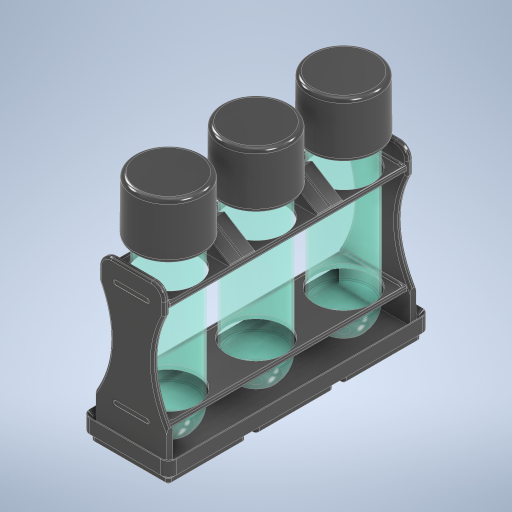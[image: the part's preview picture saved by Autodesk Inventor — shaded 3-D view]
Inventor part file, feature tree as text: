
AUTODESK INVENTOR PART (.ipt)
format: ipt  version: 2023 (Build 270158030, 158C)  size: 1,590,272 bytes
history: native  units: mm
features: extrude x23, sketch x21, other x17, fillet x17, projected_geometry x8, plane x6, chamfer x4, pattern_linear x3, mirror x2
ambient origin geometry x8: Origin, YZ Plane, XZ Plane, XY Plane, X Axis, Y Axis, Z Axis, Center Point
bodies: Body1 (feature_tree), Body2 (feature_tree), Body3 (feature_tree), Body4 (feature_tree), Body5 (feature_tree), Body6 (feature_tree), Body7 (feature_tree), Body8 (feature_tree), Body9 (feature_tree), Body10 (feature_tree), Body11 (feature_tree)
feature tree (101):
  other  "rack"
  extrude  "base-generic"  Depth=41.5mm
  extrude  "Extrusion8"  Depth=2.25mm TaperAngle=0.0deg
  extrude  "Extrusion9"  Depth=2.15mm
  extrude  "Extrusion10"  Depth=0.8mm
  extrude  "Extrusion11"  Depth=7.75mm
  extrude  "Extrusion12"  Depth=7.75mm
  plane  "Work Plane3"
  extrude  "Extrusion15"  Depth=2.4mm TaperAngle=0.0deg
  fillet  "Fillet3"  Radius=3.0mm
  extrude  "Extrusion16"  Depth=10.0mm
  fillet  "Fillet4"  Radius=2.25mm
  extrude  "Extrusion17"  Depth=35.592094mm
  fillet  "Fillet5"  Radius=15.0mm
  pattern_linear  "Rectangular Pattern1"  Spacing1=20.75mm  [1 undecoded]
  plane  "Work Plane8"
  sketch  "Sketch17"  dims[d66=7.75mm d67=2.4mm d68=0.0mm d69=3.0mm]
  extrude  "Extrusion18"  Depth=0.3mm
  pattern_linear  "Rectangular Pattern2"  Spacing1=26.75mm  [1 undecoded]
  plane  "Work Plane4"
  extrude  "Extrusion19"  Depth=2.0mm
  plane  "Work Plane6"
  extrude  "Extrusion21"  Depth=0.3mm
  extrude  "Extrusion20"  Depth=0.3mm TaperAngle=0.0deg
  fillet  "Fillet6"  Radius=9.0mm
  extrude  "Extrusion22"  Depth=0.3mm TaperAngle=0.0deg
  fillet  "Fillet7"  Radius=30.0mm
  extrude  "Extrusion28"  Depth=0.3mm
  fillet  "Fillet14"  Radius=1.0mm
  fillet  "Fillet15"  Radius=1.0mm
  pattern_linear  "Rectangular Pattern3"  Spacing1=68.75mm  [1 undecoded]
  extrude  "Extrusion23"  Depth=2.0mm
  extrude  "Extrusion24"  Depth=0.3mm
  extrude  "Extrusion25"  Depth=2.0mm TaperAngle=0.0deg
  extrude  "Extrusion26"  Depth=0.3mm
  fillet  "Fillet9"  Radius=55.0mm
  mirror  "Mirror2"
  fillet  "Fillet10"  Radius=73.0mm
  fillet  "Fillet13"  Radius=46.0mm
  extrude  "Extrusion27"  Depth=2.0mm TaperAngle=0.0deg
  chamfer  "Chamfer3"  Distance=6.0mm
  chamfer  "Chamfer4"  [1 undecoded]
  fillet  "Fillet12"  Radius=6.9mm
  fillet  "Fillet16"  Radius=6.9mm
  extrude  "Extrusion29"  Depth=0.3mm
  chamfer  "Chamfer5"  Distance=2.0mm
  chamfer  "Chamfer6"  Distance=1.0mm
  extrude  "Extrusion30"  Depth=0.3mm
  plane  "Work Plane9"
  mirror  "Mirror4"
  fillet  "Fillet19"  Radius=50.0mm
  fillet  "Fillet20"  Radius=14.0mm
  fillet  "Fillet21"  Radius=14.0mm
  fillet  "Fillet22"  Radius=3.1mm
  fillet  "Fillet18"  Radius=6.0mm
  extrude  "fill-gaps"  Depth=0.3mm
  sketch  "Sketch9"  dims[d50=41.5mm d51=41.5mm]
  sketch  "Sketch10"  dims[d52=3.75mm d53=2.25mm d54=0.0mm]
  projected_geometry  "Projected Loop2"
  sketch  "Sketch11"  dims[d55=3.75mm d56=2.15mm d57=-7.853982mm]
  projected_geometry  "Projected Loop3"
  sketch  "Sketch12"  dims[d58=1.8mm d59=0.0mm d60=0.8mm d61=-7.853982mm]
  projected_geometry  "Projected Loop4"
  sketch  "Sketch13"  dims[d62=6.5mm d63=7.75mm]
  sketch  "Sketch14"  dims[d64=7.75mm d65=7.75mm]
  sketch  "Sketch19"  dims[d70=6.0mm d71=0.0mm d72=30.0mm d74=42.0mm d75=10.0mm d77=42.0mm d79=2.25mm d80=0.0mm]
  other  "test-tube"
  sketch  "Sketch20"  dims[d82=3.75mm d84=35.592094mm d92=15.0mm]
  other  "tt-lid"
  sketch  "Sketch21"  dims[d95=12.0mm]
  other  "Pattern of test-tube:1"
  other  "TT-2"
  other  "Pattern of test-tube:2"
  other  "TT-3"
  other  "Pattern of tt-lid:3"
  other  "lid-2"
  other  "Pattern of tt-lid:4"
  other  "lid-3"
  plane  "Work Plane5"
  sketch  "Sketch23"  dims[d97=1.5mm]
  projected_geometry  "Projected Loop5"
  sketch  "Sketch25"  dims[d98=1.5mm]
  other  "tth-side"
  other  "tt-toprack"
  other  "Pattern of tt-toprack:6"
  other  "tt-rack-bottom"
  sketch  "Sketch26"  dims[d99=13.0mm]
  sketch  "Sketch28"  dims[d100=13.0mm]
  sketch  "Sketch29"  dims[d105=25.9mm]
  sketch  "Sketch30"  dims[d112=81.5mm d113=0.0mm]
  sketch  "Sketch31"  dims[d114=12.9mm]
  projected_geometry  "Projected Loop6"
  projected_geometry  "Projected Loop7"
  other  "Pattern of tth-side:7"
  other  "ttr-side-b"
  sketch  "Sketch32"  dims[d116=78.0mm]
  projected_geometry  "Projected Loop8"
  sketch  "Sketch33"  dims[d117=41.5mm]
  projected_geometry  "Projected Loop9"
  sketch  "Sketch34"  dims[d118=41.5mm]
  sketch  "Sketch35"  dims[d119=20.75mm d120=20.75mm d121=33.1mm d122=26.75mm d123=-0.087266mm d124=2.0mm d125=18.0mm d126=3.0mm d127=0.0mm d128=9.0mm d129=2.9mm d130=0.0mm d131=30.0mm d133=42.0mm d135=1.0mm d136=1.0mm d137=1.0mm d138=68.75mm d139=0.0mm d140=2.0mm d141=0.8mm d142=2.0mm d143=0.0mm d144=20.0mm d146=50.0mm d147=55.0mm d148=23.0mm d149=73.0mm d150=46.0mm d151=2.0mm d152=0.0mm d153=6.0mm d155=-3.0mm d156=6.9mm d157=6.9mm d158=2.1mm d159=2.0mm d160=0.0mm d164=1.0mm d165=2.1mm d167=50.0mm d169=14.0mm d170=14.0mm d171=3.1mm d172=6.0mm d173=3.1mm d174=6.0mm d175=0.0mm d176=0.0mm d180=3.0mm d181=0.0mm d182=4.5mm d183=0.0mm d184=1.95mm d185=0.0mm d186=3.0mm d187=12.75mm d188=12.75mm d189=6.0mm d190=0.9mm d191=1.0mm d193=2.15mm d194=4.65mm d195=0.0mm d196=1.9mm d197=2.0mm d198=45.0deg d199=0.7mm d200=2.0mm d201=45.0deg d202=0.3mm d203=0.9mm d204=1.0mm d205=1.0mm d206=1.0mm d207=1.0mm d208=1.0mm d209=0.0mm d210=2.0mm d211=0.9mm d212=0.2mm d214=15.0mm d215=15.0mm d216=15.0mm d217=15.0mm d218=10.0mm d219=0.0mm d220=14.6mm d221=9.0mm d222=30.0deg d223=14.6mm d224=9.0mm d225=30.0deg d228=5.75mm d229=5.75mm d230=0.5mm d231=5.75mm d232=5.75mm d233=0.5mm d234=0.0mm d236=0.3mm d237=0.25mm d238=0.3mm d239=0.25mm d240=0.2mm d17=0.5mm d18=0.872665mm d19=0.5mm d20=0.872665mm d24=0.0mm d25=0.0mm d26=0.0mm d27=0.0mm]
note: 4 required parameter values undecoded (feature->parameter linkage not recoverable at this tier; creation-order binding heuristic only, values carry confidence <= 0.55)
